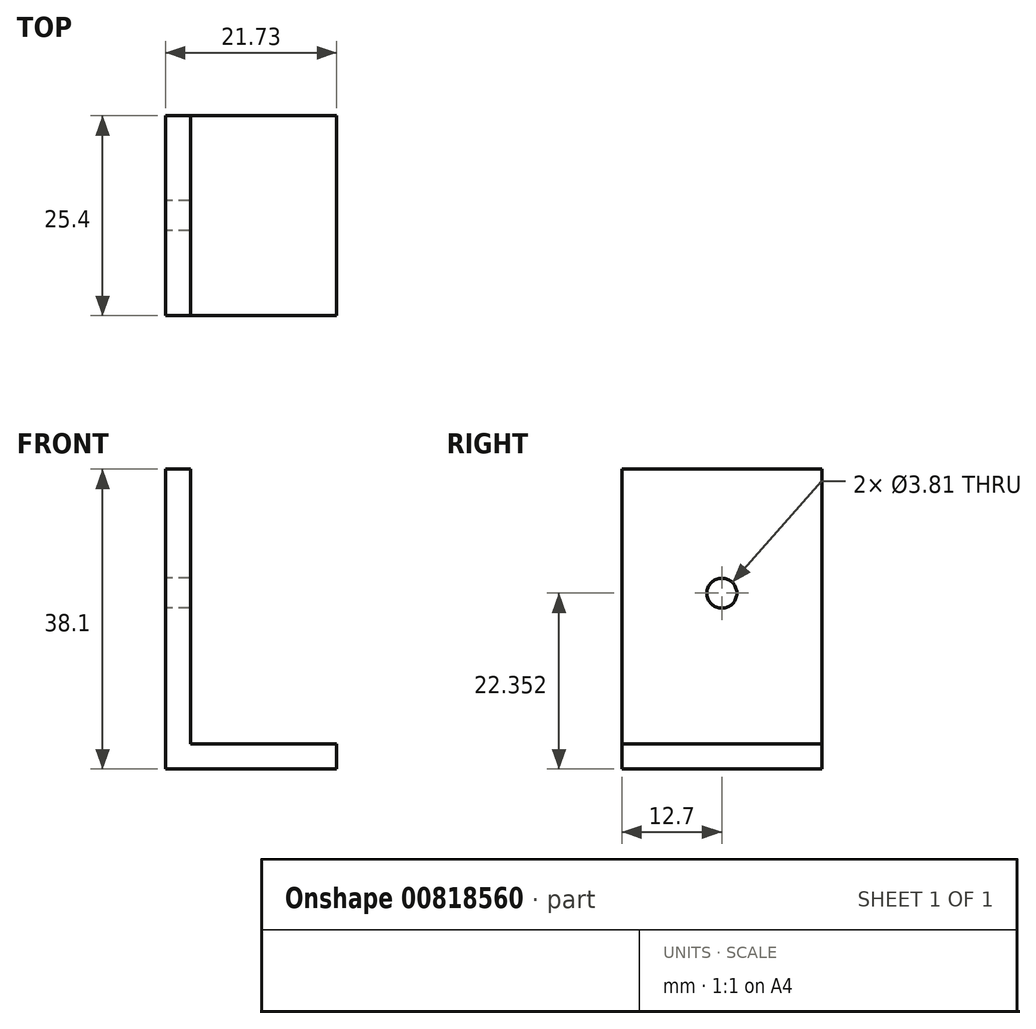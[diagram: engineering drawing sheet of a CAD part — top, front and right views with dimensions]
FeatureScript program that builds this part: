
annotation { "Feature Type Name" : "Feature", "Feature Type Description" : "" }
export const myFeature = defineFeature(function(context is Context, id is Id, definition is map)
    precondition{}
    {
        {
            var Q0;
            Q0=qCreatedBy(makeId("Front.planeOp"),FACE);
            var sketch = newSketch(context, id + "F0", { "sketchPlane" : qUnion([Q0])});
            skLineSegment(sketch, "E0", {"start": v(-21.73, 20.45) * mm, "end": v(-21.73, -17.65) * mm});
            skLineSegment(sketch, "E1", {"start": v(-21.73, -17.65) * mm, "end": v(16.37, -17.65) * mm});
            skLineSegment(sketch, "E2", {"start": v(16.37, -17.65) * mm, "end": v(16.37, -14.47) * mm});
            skLineSegment(sketch, "E3", {"start": v(16.37, -14.47) * mm, "end": v(-18.55, -14.47) * mm});
            skLineSegment(sketch, "E4", {"start": v(-18.55, -14.47) * mm, "end": v(-18.55, 20.45) * mm});
            skLineSegment(sketch, "E5", {"start": v(-18.55, 20.45) * mm, "end": v(-21.73, 20.45) * mm});
            skSolve(sketch);
        }
        {
            var Q0;
            Q0=makeQuery(id+"F0.imprint","IMPRINT",FACE,{"disambiguationData":[TD([[makeQuery(id+"F0.imprint","IMPRINT",EDGE,{"derivedFrom":sQuery(id+"F0.wireOp",EDGE,"E0")}),1.0]])]});
            extrude(context, id + "F1", {"entities" : qUnion([Q0]), "depth" : 25.4 * mm, "offsetDistance" : 25.4 * mm});
        }
        {
            var Q0;
            Q0=makeQuery(id+"F1.opExtrude","SWEPT_FACE",FACE,{"disambiguationData":[OSD([sQuery(id+"F0.wireOp",EDGE,"E1")])]});
            var sketch = newSketch(context, id + "F2", { "sketchPlane" : qUnion([Q0])});
            skLineSegment(sketch, "E6.bottom", {"start": v(16.37, 25.4) * mm, "end": v(0, 25.4) * mm});
            skLineSegment(sketch, "E6.top", {"start": v(16.37, 0) * mm, "end": v(0, 0) * mm});
            skLineSegment(sketch, "E6.left", {"start": v(16.37, 25.4) * mm, "end": v(16.37, 0) * mm});
            skLineSegment(sketch, "E6.right", {"start": v(0, 25.4) * mm, "end": v(0, 0) * mm});
            skSolve(sketch);
        }
        {
            var Q0;
            Q0 = qSketchRegion(id + "F2", true);
            extrude(context, id + "F3", {"entities" : qUnion([Q0]), "operationType" : NewBodyOperationType.REMOVE, "oppositeDirection" : true, "depth" : 25.4 * mm, "offsetDistance" : 25.4 * mm});
        }
        {
            var Q0;
            Q0=makeQuery(id+"F1.opExtrude","SWEPT_FACE",FACE,{"disambiguationData":[OSD([sQuery(id+"F0.wireOp",EDGE,"E0")])]});
            var sketch = newSketch(context, id + "F4", { "sketchPlane" : qUnion([Q0])});
            skCircle(sketch, "E7", {"center": v(12.7, 4.7) * mm, "radius": 1.9 * mm});
            skSolve(sketch);
        }
        {
            var Q0;
            Q0 = qSketchRegion(id + "F4", true);
            extrude(context, id + "F5", {"entities" : qUnion([Q0]), "operationType" : NewBodyOperationType.REMOVE, "oppositeDirection" : true, "depth" : 25.4 * mm, "offsetDistance" : 25.4 * mm});
        }
    });
